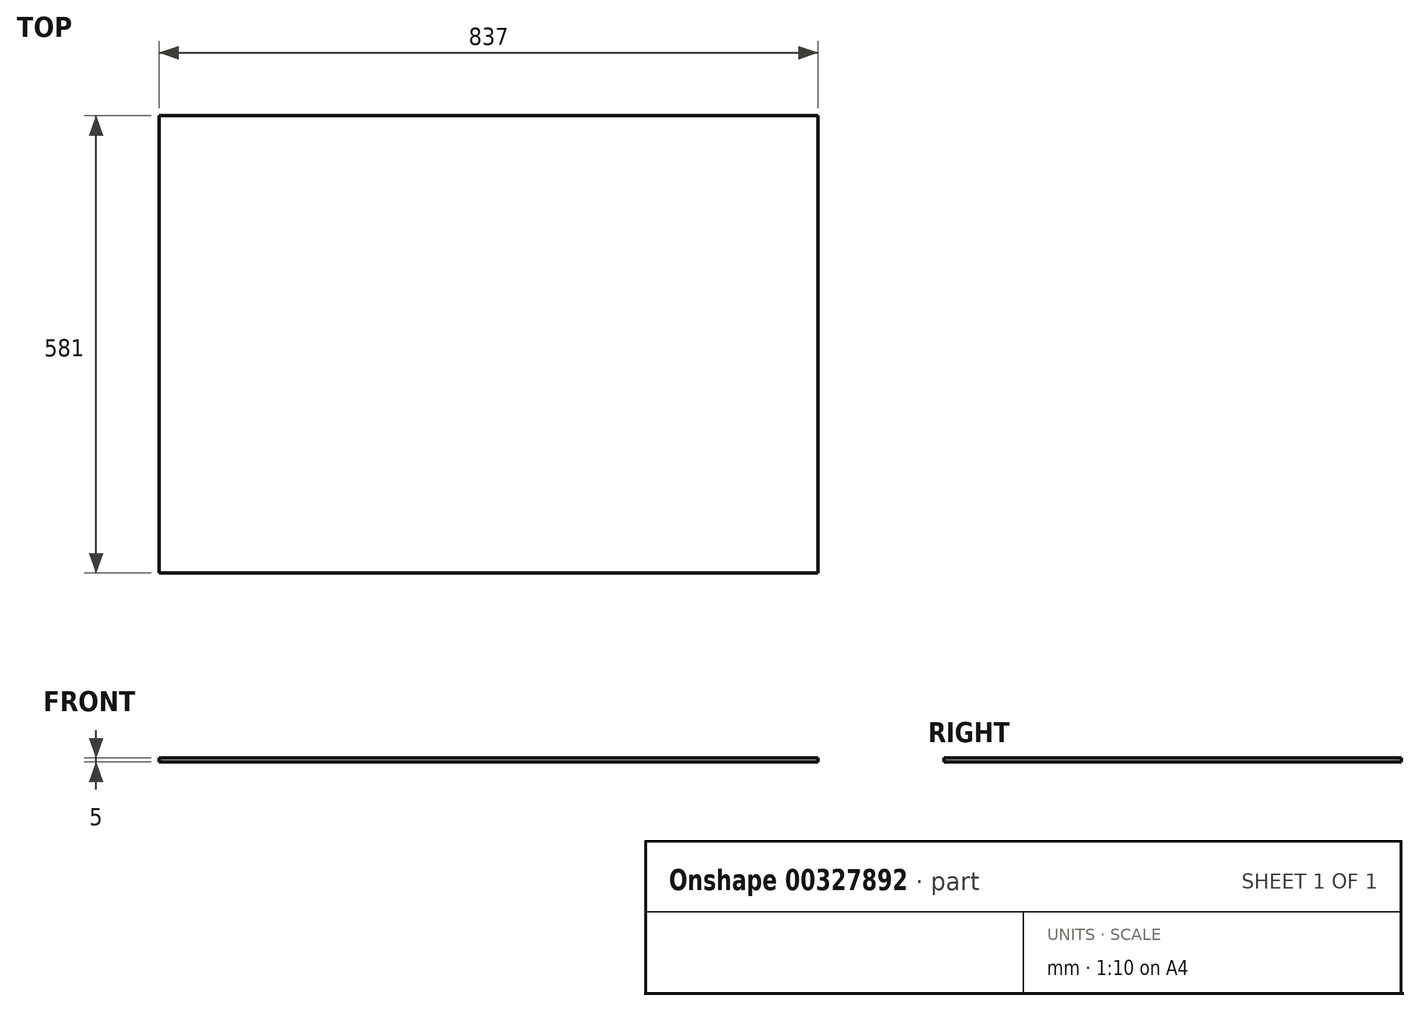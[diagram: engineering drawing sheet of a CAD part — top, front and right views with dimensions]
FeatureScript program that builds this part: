
annotation { "Feature Type Name" : "Feature", "Feature Type Description" : "" }
export const myFeature = defineFeature(function(context is Context, id is Id, definition is map)
    precondition{}
    {
        {
            var Q0;
            Q0=qCreatedBy(makeId("Top.planeOp"),FACE);
            var sketch = newSketch(context, id + "F0", { "sketchPlane" : qUnion([Q0])});
            skLineSegment(sketch, "E0.bottom", {"start": v(0, 15.46) * mm, "end": v(837, 15.46) * mm});
            skLineSegment(sketch, "E0.top", {"start": v(0, 596.46) * mm, "end": v(837, 596.46) * mm});
            skLineSegment(sketch, "E0.left", {"start": v(0, 15.46) * mm, "end": v(0, 596.46) * mm});
            skLineSegment(sketch, "E0.right", {"start": v(837, 15.46) * mm, "end": v(837, 596.46) * mm});
            skSolve(sketch);
        }
        {
            var Q0;
            Q0 = qSketchRegion(id + "F0", true);
            extrude(context, id + "F1", {"entities" : qUnion([Q0]), "depth" : 5 * mm});
        }
    });
